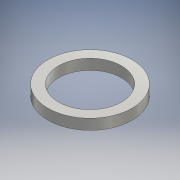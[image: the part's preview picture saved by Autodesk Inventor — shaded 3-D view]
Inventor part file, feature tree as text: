
AUTODESK INVENTOR PART (.ipt)
format: ipt  version: 2016 (Build 200138000, 138)  size: 98,304 bytes
history: native  units: mm
features: other x1, extrude x1, sketch x1
ambient origin geometry x8: Origin, YZ Plane, XZ Plane, XY Plane, X Axis, Y Axis, Z Axis, Center Point
bodies: Body1 (feature_tree)
feature tree (3):
  other  "ソリッド1"
  extrude  "押し出し1"  Depth=6.0mm
  sketch  "スケッチ1"
